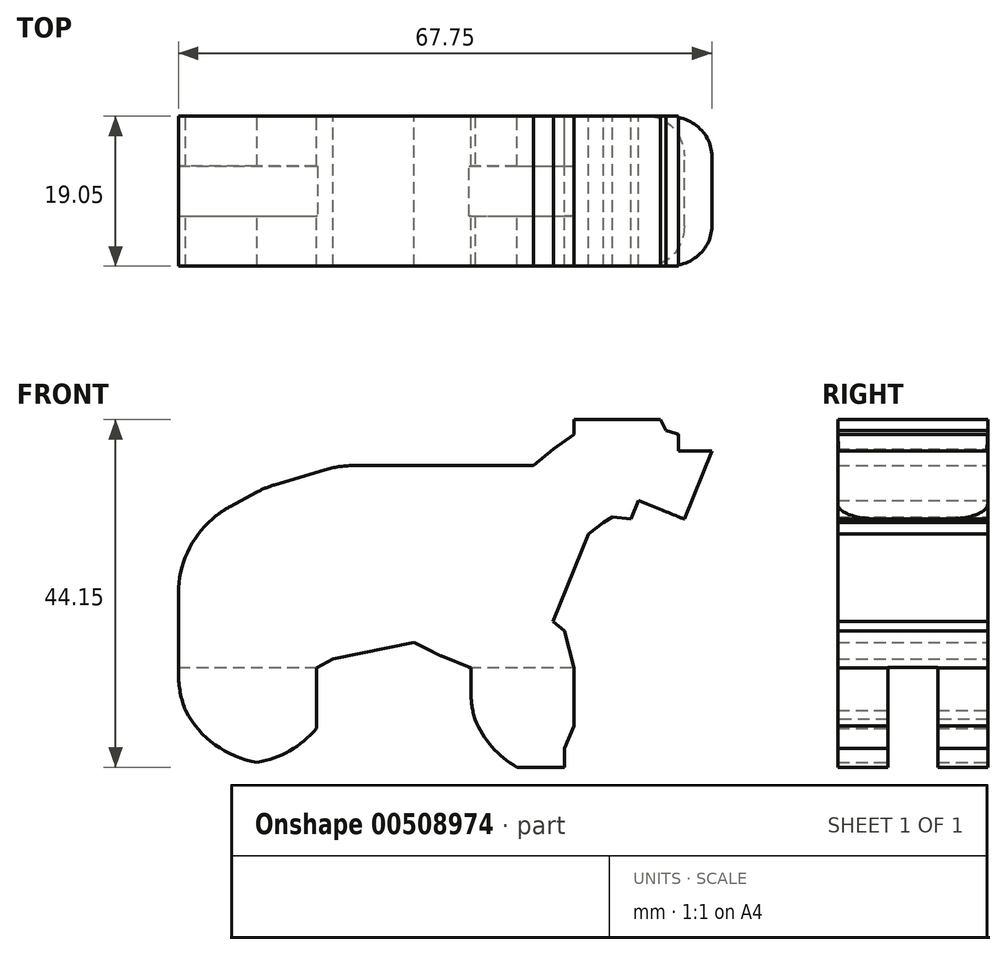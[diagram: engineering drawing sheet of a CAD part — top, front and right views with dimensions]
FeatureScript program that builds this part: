
annotation { "Feature Type Name" : "Feature", "Feature Type Description" : "" }
export const myFeature = defineFeature(function(context is Context, id is Id, definition is map)
    precondition{}
    {
        {
            var Q0;
            Q0=qCreatedBy(makeId("Front.planeOp"),FACE);
            var sketch = newSketch(context, id + "F0", { "sketchPlane" : qUnion([Q0])});
            skLineSegment(sketch, "E0", {"start": v(-34.34, 0.47) * mm, "end": v(-45.09, 0.47) * mm});
            skLineSegment(sketch, "E1", {"start": v(-45.09, 0.47) * mm, "end": v(-49.06, 9.11) * mm});
            skLineSegment(sketch, "E2", {"start": v(-49.06, 9.11) * mm, "end": v(-49.06, 14.95) * mm});
            skLineSegment(sketch, "E3", {"start": v(-49.06, 14.95) * mm, "end": v(-49.06, 27.8) * mm});
            skLineSegment(sketch, "E4", {"start": v(-49.06, 27.8) * mm, "end": v(-43.68, 32.47) * mm});
            skLineSegment(sketch, "E5", {"start": v(-43.68, 32.47) * mm, "end": v(-38.08, 35.5) * mm});
            skLineSegment(sketch, "E6", {"start": v(-38.08, 35.5) * mm, "end": v(-28.73, 38.31) * mm});
            skLineSegment(sketch, "E7", {"start": v(-28.73, 38.31) * mm, "end": v(-22.2, 38.31) * mm});
            skLineSegment(sketch, "E8", {"start": v(-22.2, 38.31) * mm, "end": v(-14.72, 38.31) * mm});
            skLineSegment(sketch, "E9", {"start": v(-14.72, 38.31) * mm, "end": v(-3.97, 38.31) * mm});
            skLineSegment(sketch, "E10", {"start": v(-3.97, 38.31) * mm, "end": v(-1.4, 40.41) * mm});
            skLineSegment(sketch, "E11", {"start": v(-1.4, 40.41) * mm, "end": v(1.17, 42.28) * mm});
            skLineSegment(sketch, "E12", {"start": v(1.17, 42.28) * mm, "end": v(1.17, 44.15) * mm});
            skLineSegment(sketch, "E13", {"start": v(1.17, 44.15) * mm, "end": v(5.37, 44.15) * mm});
            skLineSegment(sketch, "E14", {"start": v(5.37, 44.15) * mm, "end": v(8.18, 44.15) * mm});
            skLineSegment(sketch, "E15", {"start": v(8.18, 44.15) * mm, "end": v(12.15, 44.15) * mm});
            skLineSegment(sketch, "E16", {"start": v(12.15, 44.15) * mm, "end": v(12.85, 42.75) * mm});
            skLineSegment(sketch, "E17", {"start": v(12.85, 42.75) * mm, "end": v(14.48, 42.28) * mm});
            skLineSegment(sketch, "E18", {"start": v(14.48, 42.28) * mm, "end": v(14.48, 40.18) * mm});
            skLineSegment(sketch, "E19", {"start": v(14.48, 40.18) * mm, "end": v(18.69, 40.18) * mm});
            skLineSegment(sketch, "E20", {"start": v(18.69, 40.18) * mm, "end": v(15.18, 31.54) * mm});
            skLineSegment(sketch, "E21", {"start": v(15.18, 31.54) * mm, "end": v(12.85, 32.48) * mm});
            skLineSegment(sketch, "E22", {"start": v(12.85, 32.48) * mm, "end": v(9.4, 33.88) * mm});
            skLineSegment(sketch, "E23", {"start": v(9.4, 33.88) * mm, "end": v(8.45, 31.54) * mm});
            skLineSegment(sketch, "E24", {"start": v(8.45, 31.54) * mm, "end": v(6.07, 31.77) * mm});
            skLineSegment(sketch, "E25", {"start": v(6.07, 31.77) * mm, "end": v(4.9, 31.07) * mm});
            skLineSegment(sketch, "E26", {"start": v(3.04, 29.67) * mm, "end": v(-1.5, 18.5) * mm});
            skLineSegment(sketch, "E27", {"start": v(-1.5, 18.5) * mm, "end": v(0, 17.29) * mm});
            skLineSegment(sketch, "E28", {"start": v(0, 17.29) * mm, "end": v(1.17, 12.61) * mm});
            skLineSegment(sketch, "E29", {"start": v(1.17, 12.61) * mm, "end": v(1.17, 9.11) * mm});
            skLineSegment(sketch, "E30", {"start": v(1.17, 5.28) * mm, "end": v(0, 2.4) * mm});
            skLineSegment(sketch, "E31", {"start": v(0, 2.4) * mm, "end": v(0, 0) * mm});
            skLineSegment(sketch, "E32", {"start": v(0, 0) * mm, "end": v(-6.07, 0) * mm});
            skLineSegment(sketch, "E33", {"start": v(-6.07, 0) * mm, "end": v(-9.81, 1.52) * mm});
            skLineSegment(sketch, "E34", {"start": v(-11.91, 7.48) * mm, "end": v(-11.91, 9.11) * mm});
            skLineSegment(sketch, "E35", {"start": v(-11.91, 9.11) * mm, "end": v(-11.91, 12.61) * mm});
            skLineSegment(sketch, "E36", {"start": v(-11.91, 12.61) * mm, "end": v(-16.22, 14.36) * mm});
            skLineSegment(sketch, "E37", {"start": v(-16.22, 14.36) * mm, "end": v(-19.16, 15.89) * mm});
            skLineSegment(sketch, "E38", {"start": v(-31.54, 12.61) * mm, "end": v(-31.54, 9.11) * mm});
            skLineSegment(sketch, "E39", {"start": v(-31.54, 9.11) * mm, "end": v(-31.54, 4.9) * mm});
            skLineSegment(sketch, "E40", {"start": v(-31.54, 4.9) * mm, "end": v(-34.34, 0.47) * mm});
            skLineSegment(sketch, "E41", {"start": v(4.9, 31.07) * mm, "end": v(3.04, 29.67) * mm});
            skLineSegment(sketch, "E42", {"start": v(-29.43, 13.78) * mm, "end": v(-31.54, 12.61) * mm});
            skLineSegment(sketch, "E43", {"start": v(1.17, 9.11) * mm, "end": v(1.17, 5.28) * mm});
            skLineSegment(sketch, "E44", {"start": v(-19.16, 15.89) * mm, "end": v(-29.43, 13.78) * mm});
            skLineSegment(sketch, "E45", {"start": v(-11.91, 7.48) * mm, "end": v(-9.81, 1.52) * mm});
            skSolve(sketch);
        }
        {
            var Q0;
            Q0=makeQuery(id+"F0.imprint","IMPRINT",FACE,{"disambiguationData":[TD([[makeQuery(id+"F0.imprint","IMPRINT",EDGE,{"derivedFrom":sQuery(id+"F0.wireOp",EDGE,"E0")}),-1.0]])]});
            extrude(context, id + "F1", {"entities" : qUnion([Q0]), "depth" : 19.05 * mm, "offsetDistance" : 25.4 * mm});
        }
        {
            var Q0;
            Q0=makeQuery(id+"F1.opExtrude","SWEPT_EDGE",EDGE,{"disambiguationData":[OSD([sQuery(id+"F0.wireOp",EDGE,"E6"),sQuery(id+"F0.wireOp",EDGE,"E7")])]});
            var Q1;
            Q1=makeQuery(id+"F1.opExtrude","SWEPT_EDGE",EDGE,{"disambiguationData":[OSD([sQuery(id+"F0.wireOp",EDGE,"E5"),sQuery(id+"F0.wireOp",EDGE,"E6")])]});
            var Q2;
            Q2=makeQuery(id+"F1.opExtrude","SWEPT_EDGE",EDGE,{"disambiguationData":[OSD([sQuery(id+"F0.wireOp",EDGE,"E4"),sQuery(id+"F0.wireOp",EDGE,"E5")])]});
            var Q3;
            Q3=makeQuery(id+"F1.opExtrude","SWEPT_EDGE",EDGE,{"disambiguationData":[OSD([sQuery(id+"F0.wireOp",EDGE,"E3"),sQuery(id+"F0.wireOp",EDGE,"E4")])]});
            var Q4;
            Q4=makeQuery(id+"F1.opExtrude","SWEPT_EDGE",EDGE,{"disambiguationData":[OSD([sQuery(id+"F0.wireOp",EDGE,"E1"),sQuery(id+"F0.wireOp",EDGE,"E2")])]});
            var Q5;
            Q5=makeQuery(id+"F1.opExtrude","SWEPT_EDGE",EDGE,{"disambiguationData":[OSD([sQuery(id+"F0.wireOp",EDGE,"E0"),sQuery(id+"F0.wireOp",EDGE,"E1")])]});
            var Q6;
            Q6=makeQuery(id+"F1.opExtrude","SWEPT_EDGE",EDGE,{"disambiguationData":[OSD([sQuery(id+"F0.wireOp",EDGE,"E0"),sQuery(id+"F0.wireOp",EDGE,"E40")])]});
            var Q7;
            Q7=makeQuery(id+"F1.opExtrude","SWEPT_EDGE",EDGE,{"disambiguationData":[OSD([sQuery(id+"F0.wireOp",EDGE,"E36"),sQuery(id+"F0.wireOp",EDGE,"E37")])]});
            var Q8;
            Q8=makeQuery(id+"F1.opExtrude","SWEPT_EDGE",EDGE,{"disambiguationData":[OSD([sQuery(id+"F0.wireOp",EDGE,"E33"),sQuery(id+"F0.wireOp",EDGE,"E45")])]});
            var Q9;
            Q9=makeQuery(id+"F1.opExtrude","SWEPT_EDGE",EDGE,{"disambiguationData":[OSD([sQuery(id+"F0.wireOp",EDGE,"E34"),sQuery(id+"F0.wireOp",EDGE,"E45")])]});
            fillet(context, id + "F2", {"entities" : qUnion([Q0, Q1, Q2, Q3, Q4, Q5, Q6, Q7, Q8, Q9]), "radius" : 12.5 * mm, "tangentPropagation" : true, "allowEdgeOverflow" : false});
        }
        {
            var Q0;
            Q0=makeQuery(id+"F1.opExtrude","CAP_EDGE",EDGE,{"disambiguationData":[OSD([sQuery(id+"F0.wireOp",EDGE,"E20")])],"isStart":true});
            var Q1;
            Q1=makeQuery(id+"F1.opExtrude","CAP_EDGE",EDGE,{"disambiguationData":[OSD([sQuery(id+"F0.wireOp",EDGE,"E20")])],"isStart":false});
            fillet(context, id + "F3", {"entities" : qUnion([Q0, Q1]), "radius" : 5.08 * mm, "tangentPropagation" : true, "allowEdgeOverflow" : false});
        }
        {
            var Q0;
            Q0=qCreatedBy(makeId("Right.planeOp"),FACE);
            cPlane(context, id + "F4", {"entities" : qUnion([Q0]), "cplaneType" : CPlaneType.OFFSET, "offset" : 254 * mm, "width" : 152.4 * mm, "height" : 152.4 * mm});
        }
        {
            var Q0;
            Q0=qCreatedBy(id+"F4.planeOp",FACE);
            var sketch = newSketch(context, id + "F5", { "sketchPlane" : qUnion([Q0])});
            skLineSegment(sketch, "E46.0", {"start": v(-19.05, 12.61) * mm, "end": v(-19.05, 5.28) * mm});
            skLineSegment(sketch, "E47", {"start": v(0, 0) * mm, "end": v(-6.35, 0) * mm});
            skLineSegment(sketch, "E48", {"start": v(-6.35, 0) * mm, "end": v(-6.35, 12.7) * mm});
            skLineSegment(sketch, "E49", {"start": v(-6.35, 12.7) * mm, "end": v(-12.7, 12.7) * mm});
            skLineSegment(sketch, "E50", {"start": v(-12.7, 12.7) * mm, "end": v(-12.7, 0) * mm});
            skLineSegment(sketch, "E51", {"start": v(-12.7, 0) * mm, "end": v(-6.35, 0) * mm});
            skSolve(sketch);
        }
        {
            var Q0;
            Q0=makeQuery(id+"F5.imprint","IMPRINT",FACE,{"disambiguationData":[TD([[makeQuery(id+"F5.imprint","IMPRINT",EDGE,{"derivedFrom":sQuery(id+"F5.wireOp",EDGE,"E48")}),1.0]])]});
            extrude(context, id + "F6", {"entities" : qUnion([Q0]), "operationType" : NewBodyOperationType.REMOVE, "endBound" : BoundingType.THROUGH_ALL, "oppositeDirection" : true, "depth" : 25.4 * mm, "offsetDistance" : 25.4 * mm});
        }
    });
